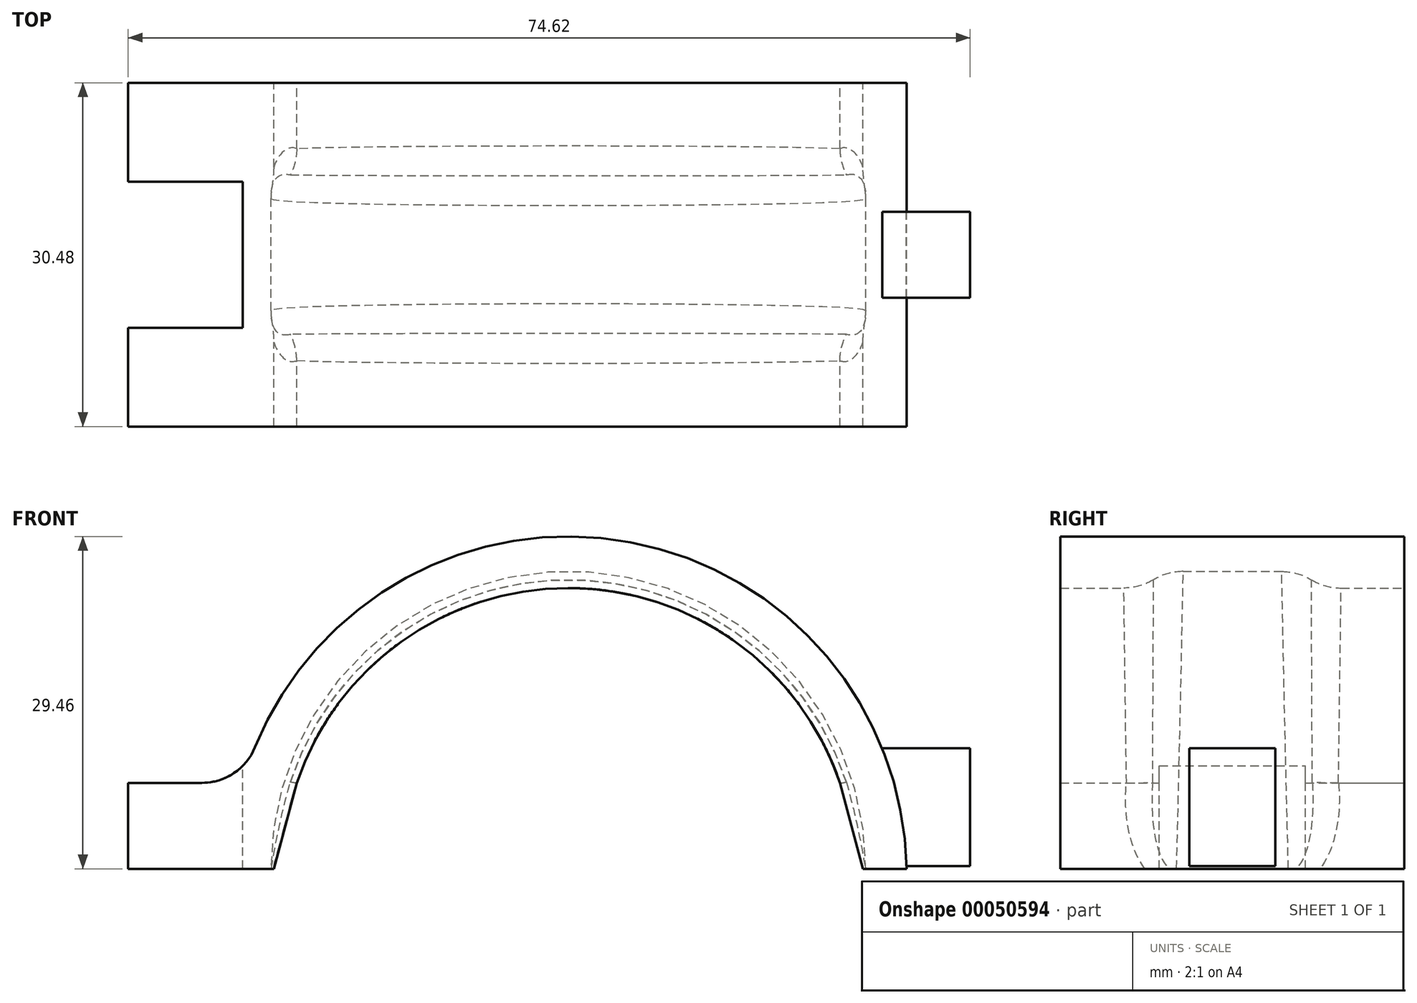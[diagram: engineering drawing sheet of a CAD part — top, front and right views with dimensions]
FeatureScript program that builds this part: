
annotation { "Feature Type Name" : "Feature", "Feature Type Description" : "" }
export const myFeature = defineFeature(function(context is Context, id is Id, definition is map)
    precondition{}
    {
        {
            var Q0;
            Q0=qCreatedBy(makeId("Front.planeOp"),FACE);
            var sketch = newSketch(context, id + "F0", { "sketchPlane" : qUnion([Q0])});
            skArc(sketch, "E0", {"start": v(24.06, 8.13) * mm, "mid": v(0, 25.4) * mm, "end": v(-24.06, 8.13) * mm});
            skLineSegment(sketch, "E1", {"start": v(-26.1, 0.5) * mm, "end": v(-39, 0.5) * mm});
            skLineSegment(sketch, "E2", {"start": v(-39, 0.5) * mm, "end": v(-39, 8.13) * mm});
            skLineSegment(sketch, "E3", {"start": v(-39, 8.13) * mm, "end": v(-28.85, 8.13) * mm});
            skLineSegment(sketch, "E4", {"start": v(26.1, 0.5) * mm, "end": v(29.97, 0.5) * mm});
            skArc(sketch, "E5", {"start": v(29.97, 0.5) * mm, "mid": v(3.85, 29.72) * mm, "end": v(-28.85, 8.13) * mm});
            skLineSegment(sketch, "E6", {"start": v(-26.1, 0.5) * mm, "end": v(-24.06, 8.13) * mm});
            skLineSegment(sketch, "E7", {"start": v(24.06, 8.13) * mm, "end": v(26.1, 0.5) * mm});
            skCircle(sketch, "E8", {"center": v(0, 0) * mm, "radius": 25.4 * mm, "construction": true});
            skSolve(sketch);
        }
        {
            var Q0;
            Q0 = qSketchRegion(id + "F0", true);
            extrude(context, id + "F1", {"entities" : qUnion([Q0]), "endBound" : BoundingType.SYMMETRIC, "depth" : 30.48 * mm});
        }
        {
            var Q0;
            Q0=makeQuery(id+"F1.opExtrude","SWEPT_EDGE",EDGE,{"disambiguationData":[OSD([sQuery(id+"F0.wireOp",EDGE,"E3"),sQuery(id+"F0.wireOp",EDGE,"E5")])]});
            var Q1;
            Q1=makeQuery(id+"F1.opExtrude","SWEPT_EDGE",EDGE,{"disambiguationData":[OSD([sQuery(id+"F0.wireOp",EDGE,"E3"),sQuery(id+"F0.wireOp",EDGE,"E5")])]});
            fillet(context, id + "F2", {"entities" : qUnion([Q0, Q1]), "radius" : 5.08 * mm, "tangentPropagation" : true, "allowEdgeOverflow" : false});
        }
        {
            var Q0;
            Q0=makeQuery(id+"F1.opExtrude","SWEPT_FACE",FACE,{"disambiguationData":[OSD([sQuery(id+"F0.wireOp",EDGE,"E3")])]});
            var sketch = newSketch(context, id + "F3", { "sketchPlane" : qUnion([Q0])});
            skLineSegment(sketch, "E9.bottom", {"start": v(-39, 6.48) * mm, "end": v(-28.85, 6.48) * mm});
            skLineSegment(sketch, "E9.top", {"start": v(-39, -6.48) * mm, "end": v(-28.85, -6.48) * mm});
            skLineSegment(sketch, "E9.left", {"start": v(-39, 6.48) * mm, "end": v(-39, -6.48) * mm});
            skLineSegment(sketch, "E9.right", {"start": v(-28.85, 6.48) * mm, "end": v(-28.85, -6.48) * mm});
            skLineSegment(sketch, "E10", {"start": v(-39, 6.48) * mm, "end": v(-39, 15.24) * mm, "construction": true});
            skLineSegment(sketch, "E11", {"start": v(-39, -15.24) * mm, "end": v(-39, -6.48) * mm, "construction": true});
            skSolve(sketch);
        }
        {
            var Q0;
            Q0 = qSketchRegion(id + "F3", true);
            extrude(context, id + "F4", {"entities" : qUnion([Q0]), "operationType" : NewBodyOperationType.REMOVE, "endBound" : BoundingType.SYMMETRIC, "oppositeDirection" : true, "depth" : 25.4 * mm});
        }
        {
            var Q0;
            Q0=makeQuery(id+"F1.opExtrude","SWEPT_FACE",FACE,{"disambiguationData":[OSD([sQuery(id+"F0.wireOp",EDGE,"E4")])]});
            var sketch = newSketch(context, id + "F5", { "sketchPlane" : qUnion([Q0])});
            skLineSegment(sketch, "E12.bottom", {"start": v(21.28, 7.94) * mm, "end": v(26.36, 7.94) * mm});
            skLineSegment(sketch, "E12.top", {"start": v(21.28, -7.94) * mm, "end": v(26.36, -7.94) * mm});
            skLineSegment(sketch, "E12.left", {"start": v(21.28, 7.94) * mm, "end": v(21.28, -7.94) * mm});
            skLineSegment(sketch, "E12.right", {"start": v(26.36, 7.94) * mm, "end": v(26.36, -7.94) * mm});
            skLineSegment(sketch, "E13", {"start": v(26.36, 7.94) * mm, "end": v(26.36, 15.24) * mm, "construction": true});
            skLineSegment(sketch, "E14", {"start": v(26.36, -7.94) * mm, "end": v(26.36, -15.24) * mm, "construction": true});
            skLineSegment(sketch, "E15", {"start": v(0, 18.42) * mm, "end": v(0, -19.6) * mm, "construction": true});
            skSolve(sketch);
        }
        {
            var Q0;
            Q0 = qSketchRegion(id + "F5", true);
            var Q1;
            Q1=sQuery(id+"F5.wireOp",EDGE,"E15");
            revolve(context, id + "F6", {"operationType" : NewBodyOperationType.REMOVE, "entities" : qUnion([Q0]), "axis" : qUnion([Q1]), "revolveType" : RevolveType.FULL, "oppositeDirection" : true});
        }
        {
            var Q0;
            Q0=makeQuery(id+"F6.boolean.opBoolean","COPY",EDGE,{"derivedFrom":makeQuery(id+"F6.opRevolve","SWEPT_EDGE",EDGE,{"disambiguationData":[OSD([sQuery(id+"F5.wireOp",EDGE,"E12.bottom"),sQuery(id+"F5.wireOp",EDGE,"E12.right")])]})});
            var Q1;
            Q1=makeQuery(id+"F6.boolean.opBoolean","COPY",EDGE,{"derivedFrom":makeQuery(id+"F6.opRevolve","SWEPT_EDGE",EDGE,{"disambiguationData":[OSD([sQuery(id+"F5.wireOp",EDGE,"E12.top"),sQuery(id+"F5.wireOp",EDGE,"E12.right")])]})});
            fillet(context, id + "F7", {"entities" : qUnion([Q0, Q1]), "radius" : 5.08 * mm, "tangentPropagation" : true, "allowEdgeOverflow" : false});
        }
        {
            var Q0;
            {var subQ2=sQuery(id+"F0.wireOp",EDGE,"E0");var subQ3=sQuery(id+"F5.wireOp",EDGE,"E12.bottom");Q0=makeQuery(id+"F7.opFillet","BLEND_EDGE",EDGE,{"blendedFrom":[makeQuery(id+"F6.boolean.opBoolean","COPY",EDGE,{"derivedFrom":makeQuery(id+"F6.opRevolve","SWEPT_EDGE",EDGE,{"disambiguationData":[OSD([subQ3,sQuery(id+"F5.wireOp",EDGE,"E12.right")])]})}),makeQuery(id+"F6.boolean.opBoolean","SPLIT",FACE,{"disambiguationData":[TD([makeQuery(id+"F6.opRevolve","SWEPT_FACE",FACE,{"disambiguationData":[OSD([subQ3])]})])],"derivedFrom":makeQuery(id+"F1.opExtrude","SWEPT_FACE",FACE,{"disambiguationData":[OSD([subQ2])]})})],"blendedInto":[makeQuery(id+"F6.boolean.opBoolean","SPLIT",FACE,{"disambiguationData":[TD([makeQuery(id+"F6.opRevolve","SWEPT_FACE",FACE,{"disambiguationData":[OSD([subQ3])]})])],"derivedFrom":makeQuery(id+"F1.opExtrude","SWEPT_FACE",FACE,{"disambiguationData":[OSD([subQ2])]})})]});}
            var Q1;
            Q1=makeQuery(id+"F6.boolean.opBoolean","INTERSECT",EDGE,{"derivedFrom":[makeQuery(id+"F1.opExtrude","SWEPT_FACE",FACE,{"disambiguationData":[OSD([sQuery(id+"F0.wireOp",EDGE,"E6")])]}),makeQuery(id+"F6.opRevolve","SWEPT_FACE",FACE,{"disambiguationData":[OSD([sQuery(id+"F5.wireOp",EDGE,"E12.bottom")])]})]});
            var Q2;
            Q2=makeQuery(id+"F6.boolean.opBoolean","INTERSECT",EDGE,{"derivedFrom":[makeQuery(id+"F1.opExtrude","SWEPT_FACE",FACE,{"disambiguationData":[OSD([sQuery(id+"F0.wireOp",EDGE,"E7")])]}),makeQuery(id+"F6.opRevolve","SWEPT_FACE",FACE,{"disambiguationData":[OSD([sQuery(id+"F5.wireOp",EDGE,"E12.bottom")])]})]});
            var Q3;
            {var subQ2=sQuery(id+"F0.wireOp",EDGE,"E0");var subQ3=sQuery(id+"F5.wireOp",EDGE,"E12.top");Q3=makeQuery(id+"F7.opFillet","BLEND_EDGE",EDGE,{"blendedFrom":[makeQuery(id+"F6.boolean.opBoolean","COPY",EDGE,{"derivedFrom":makeQuery(id+"F6.opRevolve","SWEPT_EDGE",EDGE,{"disambiguationData":[OSD([subQ3,sQuery(id+"F5.wireOp",EDGE,"E12.right")])]})}),makeQuery(id+"F6.boolean.opBoolean","SPLIT",FACE,{"disambiguationData":[TD([makeQuery(id+"F6.opRevolve","SWEPT_FACE",FACE,{"disambiguationData":[OSD([subQ3])]})])],"derivedFrom":makeQuery(id+"F1.opExtrude","SWEPT_FACE",FACE,{"disambiguationData":[OSD([subQ2])]})})],"blendedInto":[makeQuery(id+"F6.boolean.opBoolean","SPLIT",FACE,{"disambiguationData":[TD([makeQuery(id+"F6.opRevolve","SWEPT_FACE",FACE,{"disambiguationData":[OSD([subQ3])]})])],"derivedFrom":makeQuery(id+"F1.opExtrude","SWEPT_FACE",FACE,{"disambiguationData":[OSD([subQ2])]})})]});}
            var Q4;
            Q4=makeQuery(id+"F6.boolean.opBoolean","INTERSECT",EDGE,{"derivedFrom":[makeQuery(id+"F1.opExtrude","SWEPT_FACE",FACE,{"disambiguationData":[OSD([sQuery(id+"F0.wireOp",EDGE,"E7")])]}),makeQuery(id+"F6.opRevolve","SWEPT_FACE",FACE,{"disambiguationData":[OSD([sQuery(id+"F5.wireOp",EDGE,"E12.top")])]})]});
            var Q5;
            Q5=makeQuery(id+"F6.boolean.opBoolean","INTERSECT",EDGE,{"derivedFrom":[makeQuery(id+"F1.opExtrude","SWEPT_FACE",FACE,{"disambiguationData":[OSD([sQuery(id+"F0.wireOp",EDGE,"E6")])]}),makeQuery(id+"F6.opRevolve","SWEPT_FACE",FACE,{"disambiguationData":[OSD([sQuery(id+"F5.wireOp",EDGE,"E12.top")])]})]});
            var Q6;
            {var subQ1=sQuery(id+"F0.wireOp",EDGE,"E6");var subQ3=sQuery(id+"F5.wireOp",EDGE,"E12.top");Q6=makeQuery(id+"F7.opFillet","BLEND_EDGE",EDGE,{"blendedFrom":[makeQuery(id+"F6.boolean.opBoolean","COPY",EDGE,{"derivedFrom":makeQuery(id+"F6.opRevolve","SWEPT_EDGE",EDGE,{"disambiguationData":[OSD([subQ3,sQuery(id+"F5.wireOp",EDGE,"E12.right")])]})}),makeQuery(id+"F6.boolean.opBoolean","SPLIT",FACE,{"disambiguationData":[TD([makeQuery(id+"F6.opRevolve","SWEPT_FACE",FACE,{"disambiguationData":[OSD([subQ3])]})])],"derivedFrom":makeQuery(id+"F1.opExtrude","SWEPT_FACE",FACE,{"disambiguationData":[OSD([subQ1])]})})],"blendedInto":[makeQuery(id+"F6.boolean.opBoolean","SPLIT",FACE,{"disambiguationData":[TD([makeQuery(id+"F6.opRevolve","SWEPT_FACE",FACE,{"disambiguationData":[OSD([subQ3])]})])],"derivedFrom":makeQuery(id+"F1.opExtrude","SWEPT_FACE",FACE,{"disambiguationData":[OSD([subQ1])]})})]});}
            fillet(context, id + "F8", {"entities" : qUnion([Q0, Q1, Q2, Q3, Q4, Q5, Q6]), "radius" : 5.08 * mm, "tangentPropagation" : true, "allowEdgeOverflow" : false});
        }
        {
            var Q0;
            Q0=makeQuery(id+"F1.opExtrude","SWEPT_FACE",FACE,{"disambiguationData":[OSD([sQuery(id+"F0.wireOp",EDGE,"E4")])]});
            var sketch = newSketch(context, id + "F9", { "sketchPlane" : qUnion([Q0])});
            skLineSegment(sketch, "E16", {"start": v(42.77, 4.96) * mm, "end": v(26.36, 4.96) * mm});
            skLineSegment(sketch, "E17", {"start": v(26.36, 4.96) * mm, "end": v(26.32, -5.6) * mm});
            skLineSegment(sketch, "E18", {"start": v(26.32, -5.6) * mm, "end": v(42.65, -5.65) * mm});
            skLineSegment(sketch, "E19", {"start": v(42.65, -5.65) * mm, "end": v(42.77, 4.96) * mm});
            skSolve(sketch);
        }
        {
            var Q0;
            {var subQ0=sQuery(id+"F9.wireOp",EDGE,"E19");Q0=makeQuery(id+"F9.imprint","IMPRINT",FACE,{"disambiguationData":[TD([[makeQuery(id+"F9.imprint","IMPRINT",EDGE,{"derivedFrom":subQ0}),1.0]])]});}
            extrude(context, id + "F10", {"entities" : qUnion([Q0]), "oppositeDirection" : true, "depth" : 11.43 * mm});
        }
        {
            var Q0;
            Q0=makeQuery(id+"F10.opExtrude","SWEPT_BODY",BODY,{"disambiguationData":[OSD([sQuery(id+"F0.wireOp",EDGE,"E4"),sQuery(id+"F0.wireOp",EDGE,"E5"),sQuery(id+"F9.wireOp",EDGE,"E16"),sQuery(id+"F9.wireOp",EDGE,"E18"),sQuery(id+"F9.wireOp",EDGE,"E19")])]});
            deleteBodies(context, id + "F11", {"entities" : qUnion([Q0])});
        }
        {
            var Q0;
            Q0=qCreatedBy(makeId("Front.planeOp"),FACE);
            var sketch = newSketch(context, id + "F12", { "sketchPlane" : qUnion([Q0])});
            skLineSegment(sketch, "E20", {"start": v(29.96, 0.75) * mm, "end": v(35.6, 0.75) * mm});
            skLineSegment(sketch, "E21", {"start": v(35.6, 0.75) * mm, "end": v(35.6, 11.2) * mm});
            skLineSegment(sketch, "E22", {"start": v(35.6, 11.2) * mm, "end": v(27.8, 11.2) * mm});
            skLineSegment(sketch, "E23", {"start": v(27.8, 11.2) * mm, "end": v(29.96, 0.75) * mm});
            skSolve(sketch);
        }
        {
            var Q0;
            Q0=makeQuery(id+"F12.imprint","IMPRINT",FACE,{"disambiguationData":[TD([[makeQuery(id+"F12.imprint","IMPRINT",EDGE,{"derivedFrom":sQuery(id+"F12.wireOp",EDGE,"E20")}),1.0]])]});
            extrude(context, id + "F13", {"entities" : qUnion([Q0]), "operationType" : NewBodyOperationType.ADD, "endBound" : BoundingType.SYMMETRIC, "depth" : 7.62 * mm});
        }
    });
